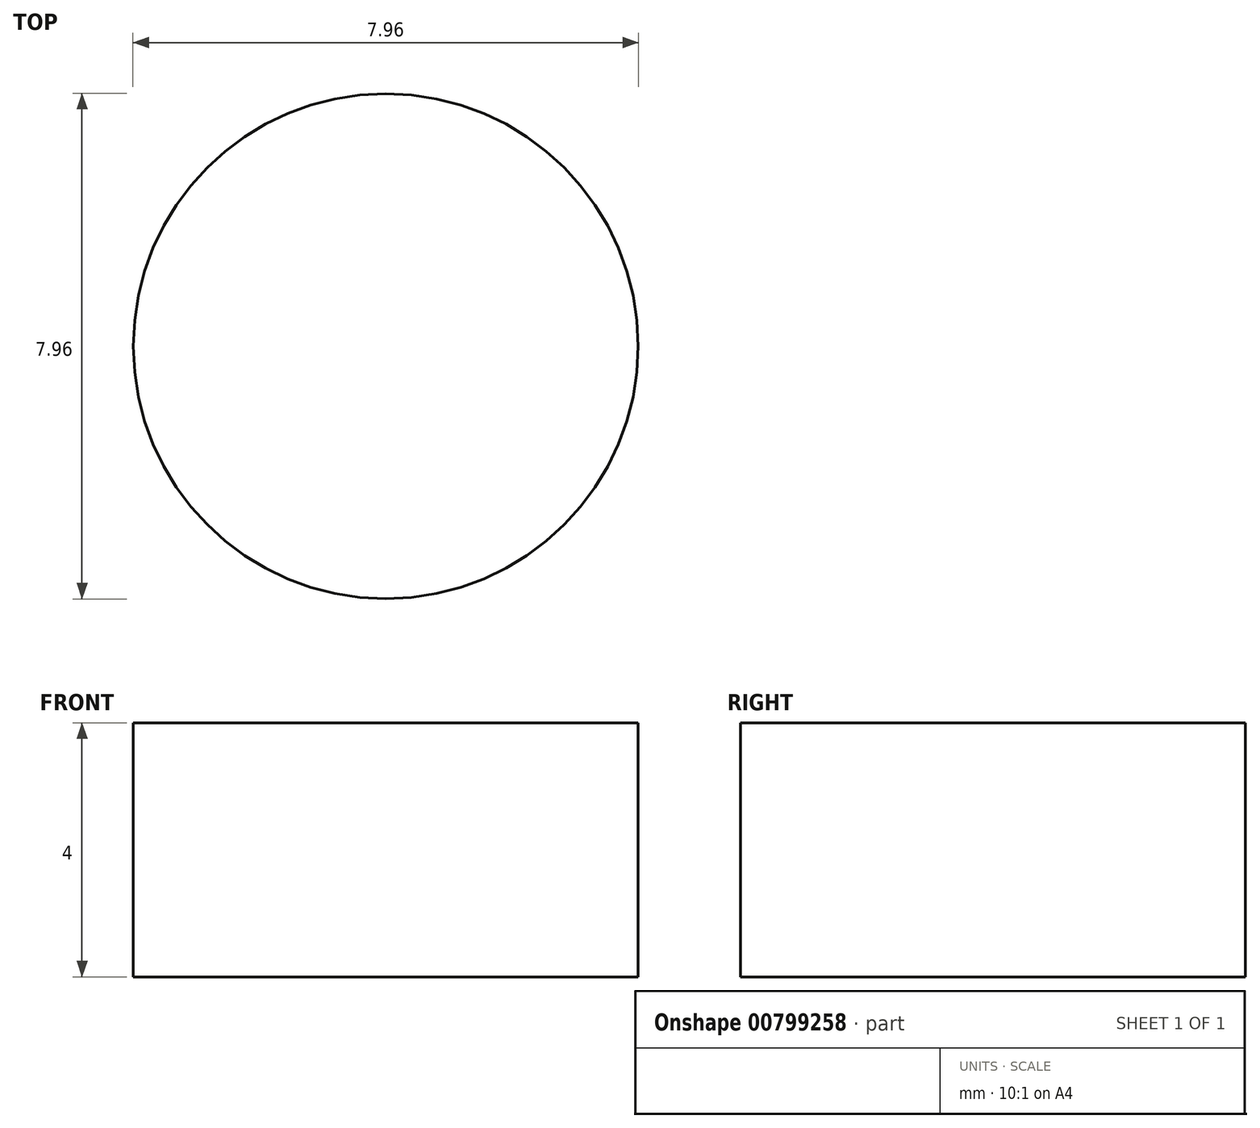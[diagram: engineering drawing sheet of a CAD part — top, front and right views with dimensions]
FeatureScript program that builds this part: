
annotation { "Feature Type Name" : "Feature", "Feature Type Description" : "" }
export const myFeature = defineFeature(function(context is Context, id is Id, definition is map)
    precondition{}
    {
        {
            var Q0;
            Q0=qCreatedBy(makeId("Top.planeOp"),FACE);
            var sketch = newSketch(context, id + "F0", { "sketchPlane" : qUnion([Q0])});
            skCircle(sketch, "E0", {"center": v(0, 0) * mm, "radius": 3.98 * mm});
            skSolve(sketch);
        }
        {
            var Q0;
            Q0 = qSketchRegion(id + "F0", true);
            extrude(context, id + "F1", {"entities" : qUnion([Q0]), "depth" : 4 * mm, "offsetDistance" : 25 * mm});
        }
    });
